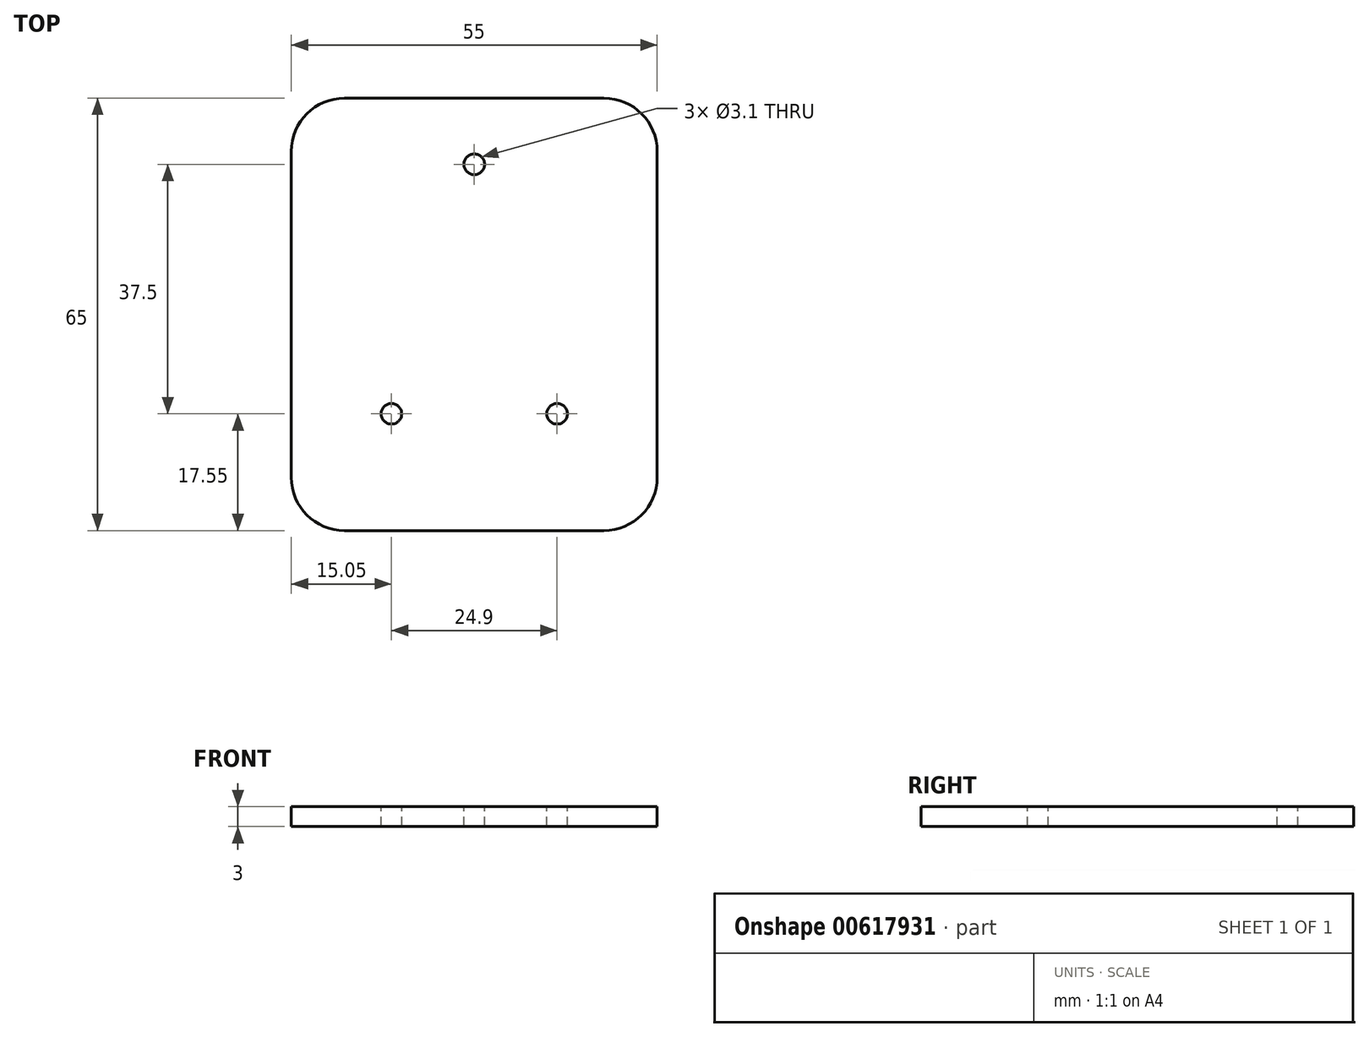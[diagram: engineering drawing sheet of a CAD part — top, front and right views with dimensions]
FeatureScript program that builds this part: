
annotation { "Feature Type Name" : "Feature", "Feature Type Description" : "" }
export const myFeature = defineFeature(function(context is Context, id is Id, definition is map)
    precondition{}
    {
        {
            var Q0;
            Q0=qCreatedBy(makeId("Top.planeOp"),FACE);
            var sketch = newSketch(context, id + "F0", { "sketchPlane" : qUnion([Q0])});
            skLineSegment(sketch, "E0.bottom", {"start": v(27.5, -32.5) * mm, "end": v(-27.5, -32.5) * mm});
            skLineSegment(sketch, "E0.top", {"start": v(27.5, 32.5) * mm, "end": v(-27.5, 32.5) * mm});
            skLineSegment(sketch, "E0.left", {"start": v(27.5, -32.5) * mm, "end": v(27.5, 32.5) * mm});
            skLineSegment(sketch, "E0.right", {"start": v(-27.5, -32.5) * mm, "end": v(-27.5, 32.5) * mm});
            skPoint(sketch, "E0.middle", {"position": v(0, 0) * mm});
            skSolve(sketch);
        }
        {
            var Q0;
            Q0=qSketchRegion(id+"F0",true);
            extrude(context, id + "F1", {"entities" : qUnion([Q0]), "depth" : 3 * mm, "offsetDistance" : 25 * mm});
        }
        {
            var Q0;
            Q0=makeQuery(id+"F1.opExtrude","CAP_FACE",FACE,{"disambiguationData":[OSD([sQuery(id+"F0.wireOp",EDGE,"E0.bottom"),sQuery(id+"F0.wireOp",EDGE,"E0.top"),sQuery(id+"F0.wireOp",EDGE,"E0.left"),sQuery(id+"F0.wireOp",EDGE,"E0.right")])],"isStart":false});
            var sketch = newSketch(context, id + "F2", { "sketchPlane" : qUnion([Q0])});
            skLineSegment(sketch, "E1", {"start": v(0, 32.5) * mm, "end": v(0, -32.5) * mm, "construction": true});
            skLineSegment(sketch, "E2", {"start": v(-27.5, 0) * mm, "end": v(27.5, 0) * mm, "construction": true});
            skCircle(sketch, "E3", {"center": v(-12.45, -14.95) * mm, "radius": 1.55 * mm});
            skCircle(sketch, "E4", {"center": v(12.45, -14.95) * mm, "radius": 1.55 * mm});
            skCircle(sketch, "E5", {"center": v(0, 22.55) * mm, "radius": 1.55 * mm});
            skLineSegment(sketch, "E6", {"start": v(-12.45, -14.95) * mm, "end": v(12.45, -14.95) * mm, "construction": true});
            skPoint(sketch, "E7", {"position": v(0, -14.95) * mm});
            skLineSegment(sketch, "E8.bottom", {"start": v(15, -17.5) * mm, "end": v(-15, -17.5) * mm, "construction": true});
            skLineSegment(sketch, "E8.top", {"start": v(15, 25.1) * mm, "end": v(-15, 25.1) * mm, "construction": true});
            skLineSegment(sketch, "E8.left", {"start": v(15, -17.5) * mm, "end": v(15, 25.1) * mm, "construction": true});
            skLineSegment(sketch, "E8.right", {"start": v(-15, -17.5) * mm, "end": v(-15, 25.1) * mm, "construction": true});
            skPoint(sketch, "E8.middle", {"position": v(0, 3.8) * mm});
            skSolve(sketch);
        }
        {
            var Q0;
            Q0=qSketchRegion(id+"F2",true);
            var Q1;
            Q1=makeQuery(id+"F1.opExtrude","CAP_FACE",FACE,{"disambiguationData":[OSD([sQuery(id+"F0.wireOp",EDGE,"E0.bottom"),sQuery(id+"F0.wireOp",EDGE,"E0.top"),sQuery(id+"F0.wireOp",EDGE,"E0.left"),sQuery(id+"F0.wireOp",EDGE,"E0.right")])],"isStart":true});
            extrude(context, id + "F3", {"entities" : qUnion([Q0]), "operationType" : NewBodyOperationType.REMOVE, "endBound" : BoundingType.UP_TO_SURFACE, "oppositeDirection" : true, "depth" : 25 * mm, "endBoundEntityFace" : qUnion([Q1]), "offsetDistance" : 25 * mm});
        }
        {
            var Q0;
            Q0=makeQuery(id+"F1.opExtrude","SWEPT_EDGE",EDGE,{"disambiguationData":[OSD([sQuery(id+"F0.wireOp",EDGE,"E0.bottom"),sQuery(id+"F0.wireOp",EDGE,"E0.left")])]});
            var Q1;
            Q1=makeQuery(id+"F1.opExtrude","SWEPT_EDGE",EDGE,{"disambiguationData":[OSD([sQuery(id+"F0.wireOp",EDGE,"E0.bottom"),sQuery(id+"F0.wireOp",EDGE,"E0.right")])]});
            var Q2;
            Q2=makeQuery(id+"F1.opExtrude","SWEPT_EDGE",EDGE,{"disambiguationData":[OSD([sQuery(id+"F0.wireOp",EDGE,"E0.top"),sQuery(id+"F0.wireOp",EDGE,"E0.right")])]});
            var Q3;
            Q3=makeQuery(id+"F1.opExtrude","SWEPT_EDGE",EDGE,{"disambiguationData":[OSD([sQuery(id+"F0.wireOp",EDGE,"E0.top"),sQuery(id+"F0.wireOp",EDGE,"E0.left")])]});
            fillet(context, id + "F4", {"entities" : qUnion([Q0, Q1, Q2, Q3]), "radius" : 8 * mm, "tangentPropagation" : true, "allowEdgeOverflow" : false});
        }
    });
